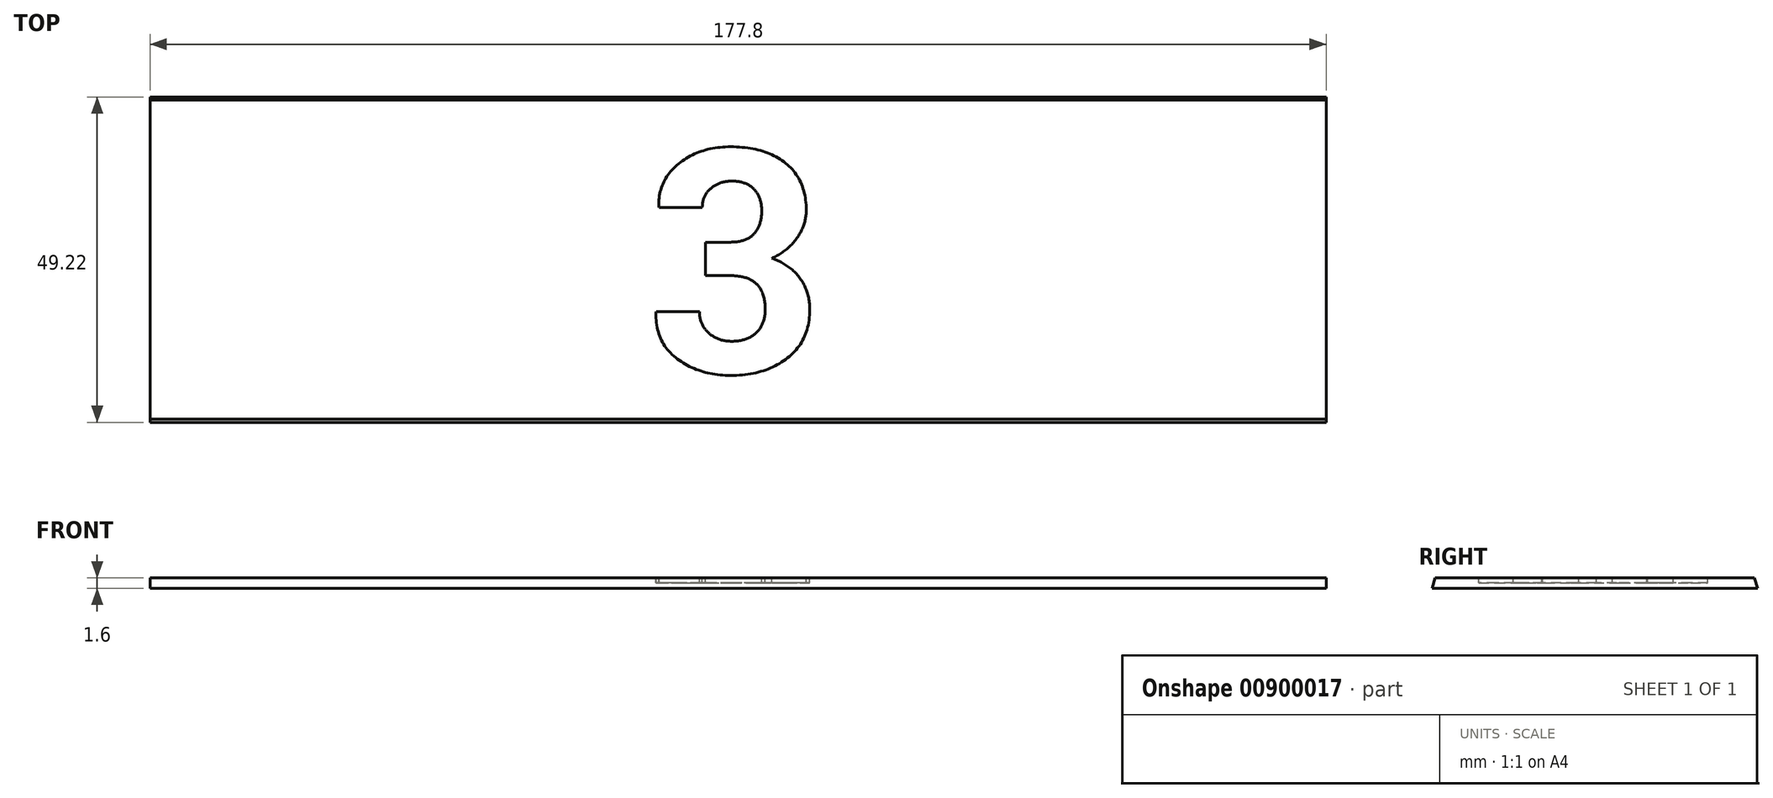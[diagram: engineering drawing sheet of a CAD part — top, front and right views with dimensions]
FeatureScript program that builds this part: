
annotation { "Feature Type Name" : "Feature", "Feature Type Description" : "" }
export const myFeature = defineFeature(function(context is Context, id is Id, definition is map)
    precondition{}
    {
        {
            var Q0;
            Q0=qCreatedBy(makeId("Top.planeOp"),FACE);
            var sketch = newSketch(context, id + "F0", { "sketchPlane" : qUnion([Q0])});
            skLineSegment(sketch, "E0", {"start": v(-88.9, 24.6) * mm, "end": v(88.9, 24.6) * mm});
            skLineSegment(sketch, "E1", {"start": v(88.9, 24.6) * mm, "end": v(88.9, -24.6) * mm});
            skLineSegment(sketch, "E2", {"start": v(88.9, -24.6) * mm, "end": v(-88.9, -24.6) * mm});
            skLineSegment(sketch, "E3", {"start": v(-88.9, -24.6) * mm, "end": v(-88.9, 24.6) * mm});
            skLineSegment(sketch, "E4", {"start": v(-88.9, 24.6) * mm, "end": v(88.9, -24.6) * mm, "construction": true});
            skPoint(sketch, "E5", {"position": v(0, 0) * mm});
            skSolve(sketch);
        }
        {
            var Q0;
            Q0 = qSketchRegion(id + "F0", true);
            extrude(context, id + "F1", {"entities" : qUnion([Q0]), "depth" : 1.6 * mm, "offsetDistance" : 25.4 * mm});
        }
        {
            var Q0;
            Q0=makeQuery(id+"F1.opExtrude","SWEPT_FACE",FACE,{"disambiguationData":[OSD([sQuery(id+"F0.wireOp",EDGE,"E1")])]});
            var sketch = newSketch(context, id + "F2", { "sketchPlane" : qUnion([Q0])});
            skLineSegment(sketch, "E6", {"start": v(-24.6, 0) * mm, "end": v(-24.13, 1.6) * mm});
            skLineSegment(sketch, "E7", {"start": v(-24.13, 1.6) * mm, "end": v(-24.6, 1.6) * mm});
            skLineSegment(sketch, "E8", {"start": v(-24.6, 1.6) * mm, "end": v(-24.6, 0) * mm});
            skLineSegment(sketch, "E9", {"start": v(24.6, 1.6) * mm, "end": v(24.13, 1.6) * mm});
            skLineSegment(sketch, "E10", {"start": v(24.13, 1.6) * mm, "end": v(24.6, 0) * mm});
            skLineSegment(sketch, "E11", {"start": v(24.6, 0) * mm, "end": v(24.6, 1.6) * mm});
            skSolve(sketch);
        }
        {
            var Q0;
            Q0 = qSketchRegion(id + "F2", true);
            extrude(context, id + "F3", {"entities" : qUnion([Q0]), "operationType" : NewBodyOperationType.REMOVE, "endBound" : BoundingType.THROUGH_ALL, "oppositeDirection" : true, "depth" : 25.4 * mm, "offsetDistance" : 25.4 * mm});
        }
        {
            var Q0;
            Q0=makeQuery(id+"F1.opExtrude","CAP_FACE",FACE,{"disambiguationData":[OSD([sQuery(id+"F0.wireOp",EDGE,"E0"),sQuery(id+"F0.wireOp",EDGE,"E1"),sQuery(id+"F0.wireOp",EDGE,"E2"),sQuery(id+"F0.wireOp",EDGE,"E3")])],"isStart":false});
            var sketch = newSketch(context, id + "F4", { "sketchPlane" : qUnion([Q0])});
            skText(sketch, "E12", { "text": "3", "fontName": "RobotoSlab-Bold.ttf"});
            skPoint(sketch, "E13", {"position": v(0, 0) * mm});
            const initialGuessF4  = {"E12": [-0.01373, -0.01702, 1, 0, 0.03404]};
            skSetInitialGuess(sketch, initialGuessF4);
            skSolve(sketch);
        }
        {
            var Q0;
            Q0 = qSketchRegion(id + "F4", true);
            extrude(context, id + "F5", {"entities" : qUnion([Q0]), "operationType" : NewBodyOperationType.REMOVE, "oppositeDirection" : true, "depth" : 0.79 * mm, "offsetDistance" : 25.4 * mm});
        }
    });
